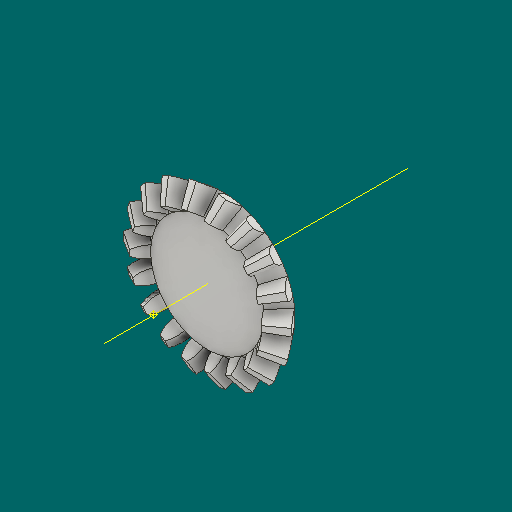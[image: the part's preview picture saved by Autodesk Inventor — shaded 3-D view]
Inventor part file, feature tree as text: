
AUTODESK INVENTOR PART (.ipt)
format: ipt  version: 2023.1 (Build 271208000, 208)  size: 475,136 bytes
history: native  units: mm
features: other x24, loft x2, pattern_circular x2, sketch x1
ambient origin geometry x6: Origin, XZ Plane, X Axis, Y Axis, Z Axis, Center Point
bodies: Solid1 (feature_tree)
feature tree (29):
  other  "Top Point"
  other  "Mesh Plane2"
  other  "Teeth Body"
  other  "Start Point"
  other  "Tooth Plane"
  other  "Start Sketch"
  other  "End Point"
  other  "3D Sketch Right"
  other  "End Plane Right"
  loft  "Loft Right"
  pattern_circular  "Circular Pattern Right"  [2 undecoded]
  other  "3D Sketch Left"
  other  "End Plane Left"
  loft  "Loft Left"
  pattern_circular  "Circular Pattern Left"  [2 undecoded]
  other  "Fix Body"
  other  "Mesh Plane"
  other  "Top Plane"
  other  "Teeth Body Sketch"
  other  "End Plane"
  other  "End Sketch"
  other  "Helical Curve Left"
  other  "End Sketch Left"
  other  "Body Sketch"
  sketch  "Sketch6"  dims[d0=22.86mm d1=20.988709mm d2=24.419409mm d3=3.175mm d4=7.887523mm d5=90.0deg d7=5.237059mm d8=5.962066mm d9=16.924983mm d11=3.3147mm d12=4.038232mm d15=4.597277mm d16=13.050649mm d17=0.0mm d18=90.0deg d19=0.0mm d20=90.0deg d21=180.0mm d22=360.0deg d26=111.138613mm d27=2.035029mm d28=22.86mm d29=-9.097532mm d30=4.038232mm d31=4.597277mm d32=13.050649mm d35=0.0mm d37=0.0mm d39=0.0mm d40=90.0deg d41=180.0mm d42=360.0deg d46=90.0deg d47=90.0deg d48=0.0mm d49=0.0mm d50=90.0deg d51=1.745329mm d52=0.0mm d53=0.0mm d54=0.0mm d56=5.857279mm d57=20.725636mm d58=16.758156mm d59=15.981286mm d60=12.92201mm d61=15.981286mm d62=12.92201mm d63=90.0deg d64=90.0deg d65=111.138613mm d66=31.5mm d67=22.86mm d68=-9.097532mm d69=2.035029mm d70=4.597277mm d71=13.050649mm d72=4.038232mm d73=12.92201mm d74=15.981286mm d75=0.0mm d76=90.0deg d77=0.0mm d78=90.0deg d79=0.0mm d80=90.0deg d81=180.0mm d82=360.0deg d84=10.0mm d85=20.0mm d86=20.0mm d87=10.0mm d88=0.0mm d89=0.0mm]
  other  "Srf1"
  other  "Helical Curve Right"
  other  "End Sketch Right"
  other  "Pitch Diameter"
note: 4 required parameter values undecoded (feature->parameter linkage not recoverable at this tier; creation-order binding heuristic only, values carry confidence <= 0.55)
